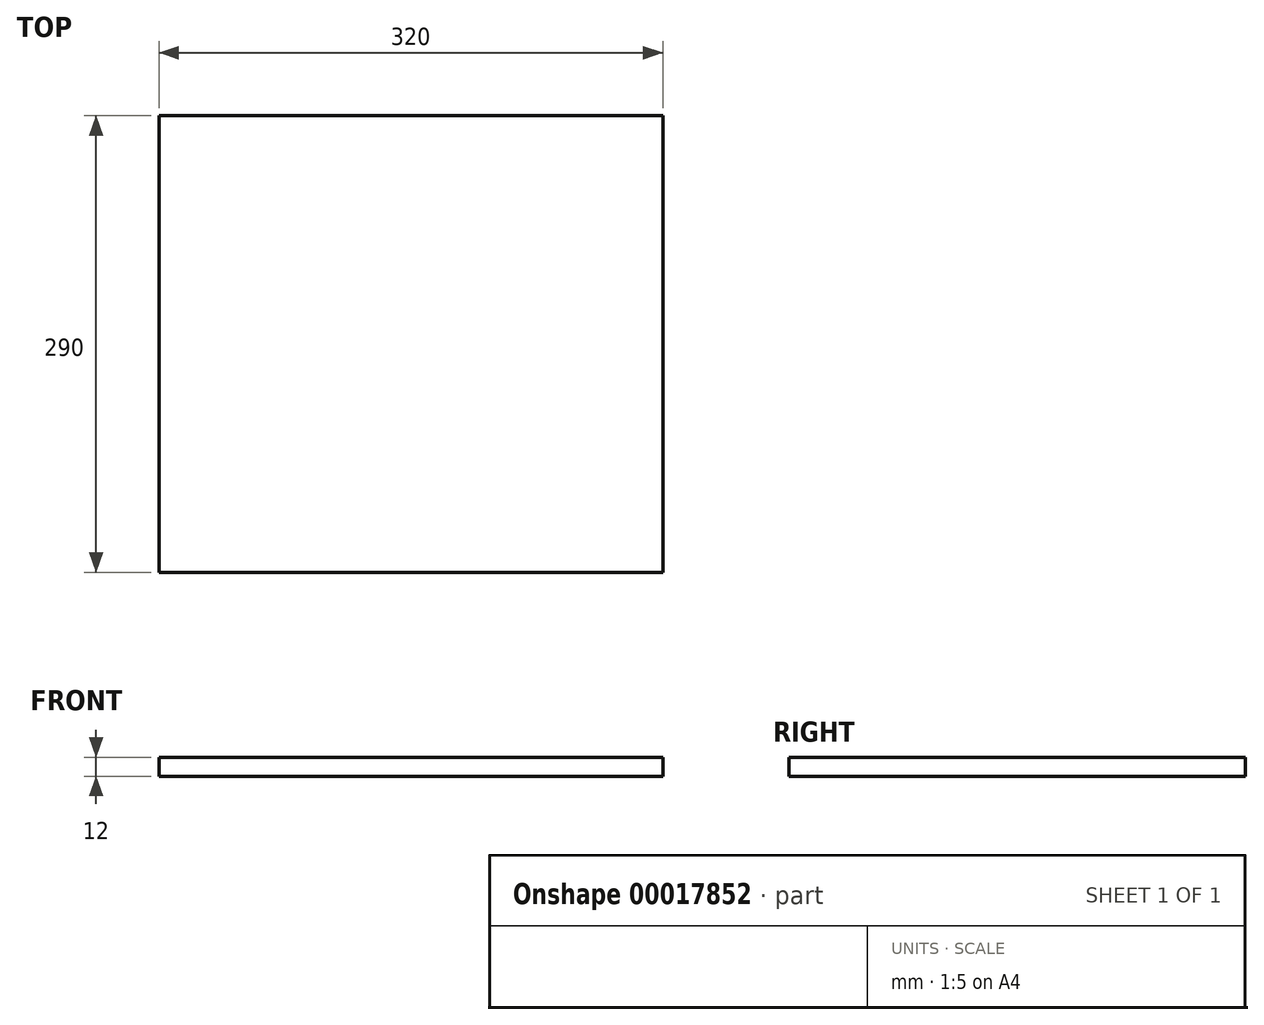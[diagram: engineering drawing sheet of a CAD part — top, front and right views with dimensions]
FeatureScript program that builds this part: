
annotation { "Feature Type Name" : "Feature", "Feature Type Description" : "" }
export const myFeature = defineFeature(function(context is Context, id is Id, definition is map)
    precondition{}
    {
        {
            var Q0;
            Q0=qCreatedBy(makeId("Top.planeOp"),FACE);
            var sketch = newSketch(context, id + "F0", { "sketchPlane" : qUnion([Q0])});
            skLineSegment(sketch, "E0.bottom", {"start": v(-70.96, 65.05) * mm, "end": v(249.04, 65.05) * mm});
            skLineSegment(sketch, "E0.top", {"start": v(-70.96, -224.95) * mm, "end": v(249.04, -224.95) * mm});
            skLineSegment(sketch, "E0.left", {"start": v(-70.96, 65.05) * mm, "end": v(-70.96, -224.95) * mm});
            skLineSegment(sketch, "E0.right", {"start": v(249.04, 65.05) * mm, "end": v(249.04, -224.95) * mm});
            skSolve(sketch);
        }
        {
            var Q0;
            Q0=qSketchRegion(id+"F0",true);
            extrude(context, id + "F1", {"entities" : qUnion([Q0]), "depth" : 12 * mm});
        }
    });
